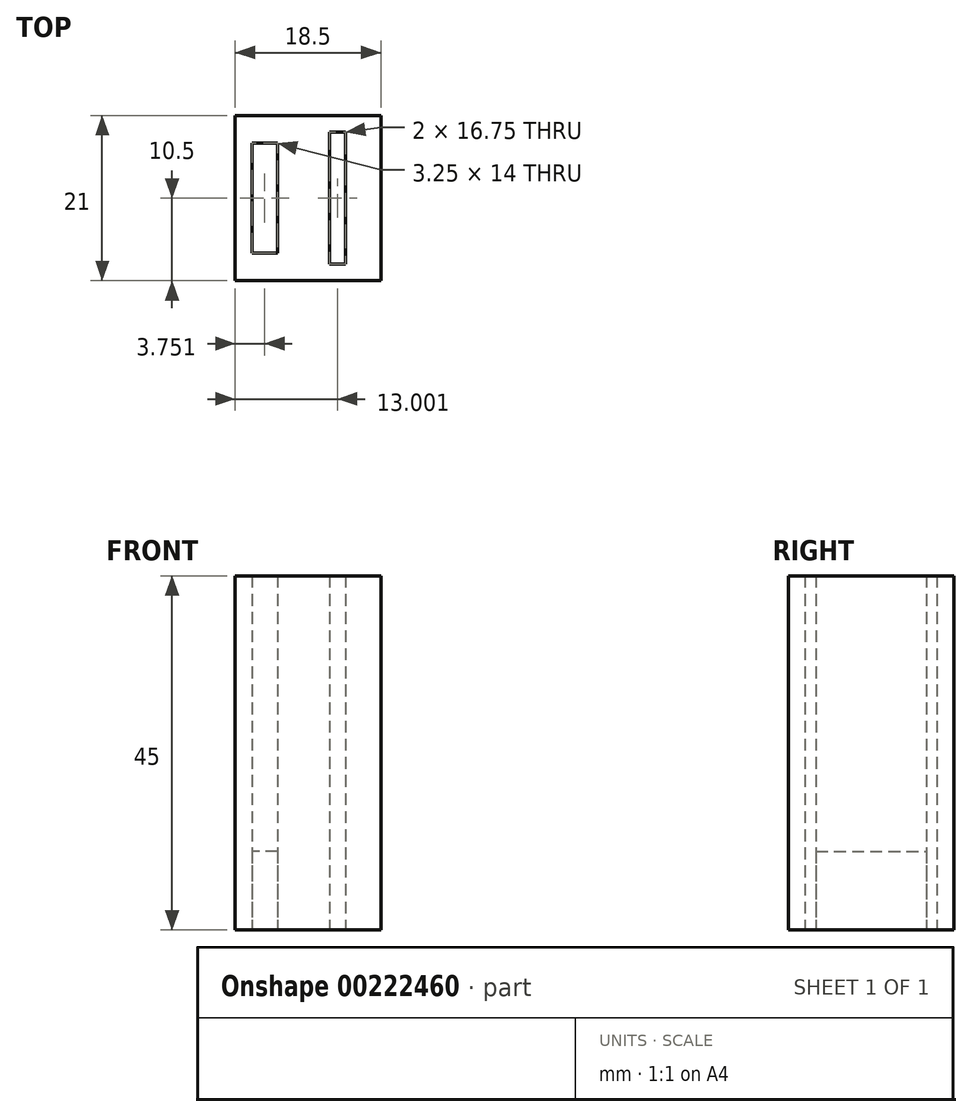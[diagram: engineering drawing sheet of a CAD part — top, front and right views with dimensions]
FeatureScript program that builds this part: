
annotation { "Feature Type Name" : "Feature", "Feature Type Description" : "" }
export const myFeature = defineFeature(function(context is Context, id is Id, definition is map)
    precondition{}
    {
        {
            var Q0;
            Q0=qCreatedBy(makeId("Top.planeOp"),FACE);
            var sketch = newSketch(context, id + "F0", { "sketchPlane" : qUnion([Q0])});
            skLineSegment(sketch, "E0.bottom", {"start": v(-18.34, 10.18) * mm, "end": v(-10.84, 10.18) * mm});
            skLineSegment(sketch, "E0.top", {"start": v(-18.34, -10.82) * mm, "end": v(-10.84, -10.82) * mm});
            skLineSegment(sketch, "E0.left", {"start": v(-18.34, 10.18) * mm, "end": v(-18.34, -10.82) * mm});
            skLineSegment(sketch, "E0.right", {"start": v(-10.84, 10.18) * mm, "end": v(-10.84, -10.82) * mm});
            skLineSegment(sketch, "E1.bottom", {"start": v(-10.84, -10.82) * mm, "end": v(0.16, -10.82) * mm});
            skLineSegment(sketch, "E1.top", {"start": v(-10.84, 10.18) * mm, "end": v(0.16, 10.18) * mm});
            skLineSegment(sketch, "E1.left", {"start": v(-10.84, -10.82) * mm, "end": v(-10.84, 10.18) * mm});
            skLineSegment(sketch, "E1.right", {"start": v(0.16, -10.82) * mm, "end": v(0.16, 10.18) * mm});
            skPoint(sketch, "E2", {"position": v(-14.59, 10.18) * mm});
            skPoint(sketch, "E3", {"position": v(-18.34, -0.32) * mm});
            skPoint(sketch, "E4", {"position": v(-5.34, 10.18) * mm});
            skLineSegment(sketch, "E5", {"start": v(-14.59, 10.18) * mm, "end": v(-14.59, -12.32) * mm, "construction": true});
            skLineSegment(sketch, "E6", {"start": v(-5.34, 10.18) * mm, "end": v(-5.34, -12.72) * mm, "construction": true});
            skLineSegment(sketch, "E7", {"start": v(-18.34, -0.32) * mm, "end": v(5.69, -0.32) * mm, "construction": true});
            skLineSegment(sketch, "E8.bottom", {"start": v(-12.96, -7.32) * mm, "end": v(-16.21, -7.32) * mm});
            skLineSegment(sketch, "E8.top", {"start": v(-12.96, 6.68) * mm, "end": v(-16.21, 6.68) * mm});
            skLineSegment(sketch, "E8.left", {"start": v(-12.96, -7.32) * mm, "end": v(-12.96, 6.68) * mm});
            skLineSegment(sketch, "E8.right", {"start": v(-16.21, -7.32) * mm, "end": v(-16.21, 6.68) * mm});
            skPoint(sketch, "E8.middle", {"position": v(-14.59, -0.32) * mm});
            skLineSegment(sketch, "E9.bottom", {"start": v(-4.34, -8.7) * mm, "end": v(-6.34, -8.7) * mm});
            skLineSegment(sketch, "E9.top", {"start": v(-4.34, 8.06) * mm, "end": v(-6.34, 8.06) * mm});
            skLineSegment(sketch, "E9.left", {"start": v(-4.34, -8.7) * mm, "end": v(-4.34, 8.06) * mm});
            skLineSegment(sketch, "E9.right", {"start": v(-6.34, -8.7) * mm, "end": v(-6.34, 8.06) * mm});
            skPoint(sketch, "E9.middle", {"position": v(-5.34, -0.32) * mm});
            skSolve(sketch);
        }
        {
            var Q0;
            Q0=makeQuery(id+"F0.imprint","IMPRINT",FACE,{"disambiguationData":[TD([[makeQuery(id+"F0.imprint","IMPRINT",EDGE,{"derivedFrom":sQuery(id+"F0.wireOp",EDGE,"E8.bottom")}),-1.0]])]});
            extrude(context, id + "F1", {"entities" : qUnion([Q0]), "depth" : 10 * mm});
        }
        {
            var Q0;
            Q0=makeQuery(id+"F0.imprint","IMPRINT",FACE,{"disambiguationData":[TD([[makeQuery(id+"F0.imprint","IMPRINT",EDGE,{"derivedFrom":sQuery(id+"F0.wireOp",EDGE,"E1.bottom")}),1.0]])]});
            var Q1;
            Q1=makeQuery(id+"F0.imprint","IMPRINT",FACE,{"disambiguationData":[TD([[makeQuery(id+"F0.imprint","IMPRINT",EDGE,{"derivedFrom":sQuery(id+"F0.wireOp",EDGE,"E0.bottom")}),-1.0]])]});
            extrude(context, id + "F2", {"entities" : qUnion([Q0, Q1]), "depth" : 45 * mm});
        }
    });
